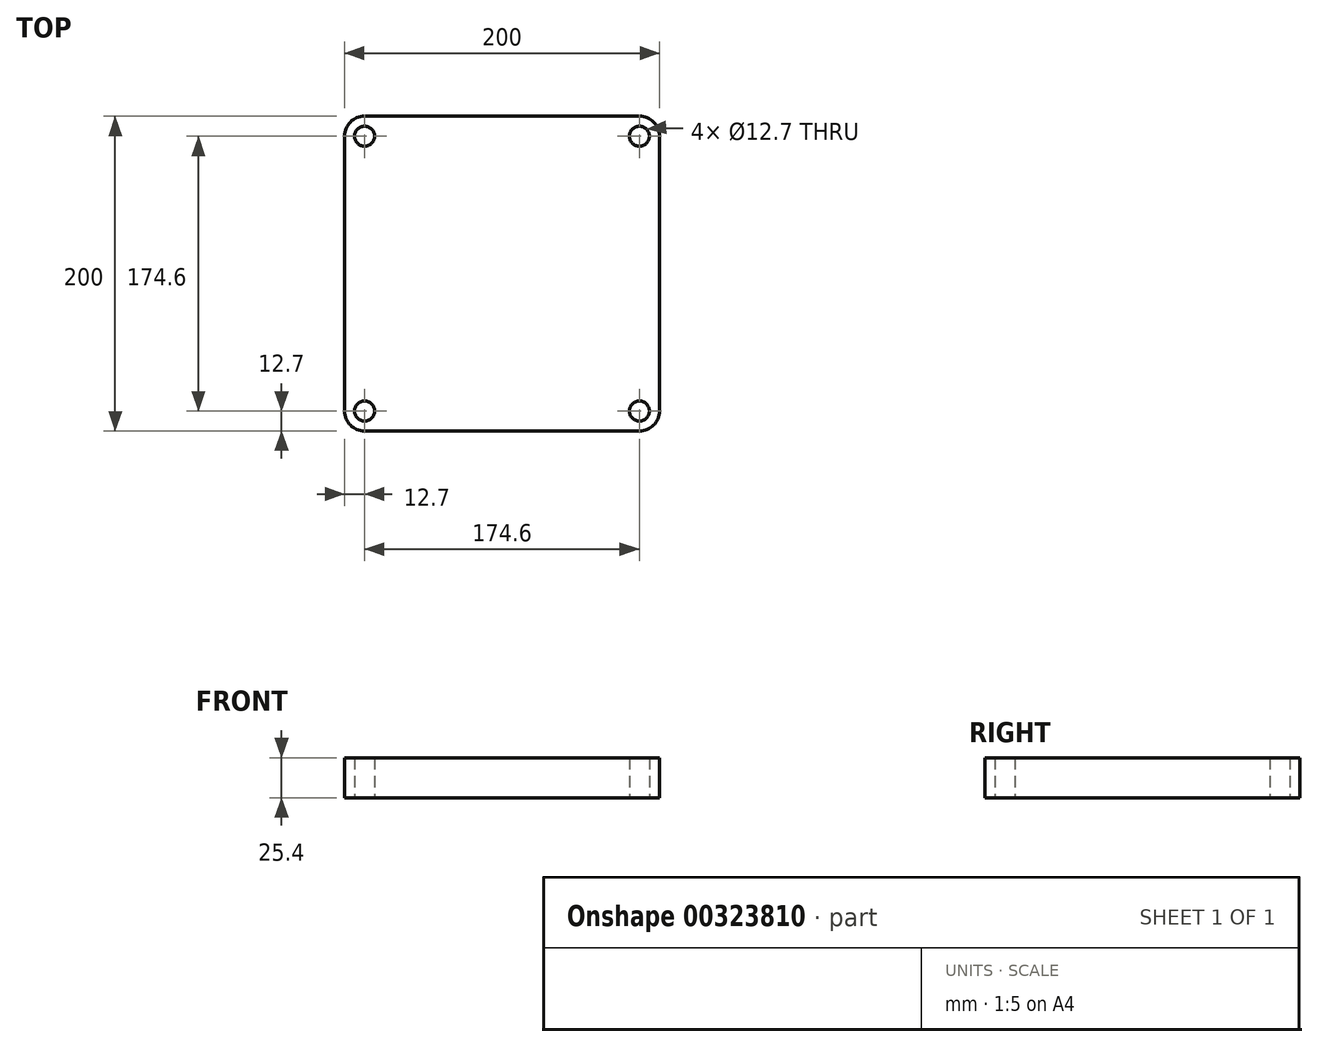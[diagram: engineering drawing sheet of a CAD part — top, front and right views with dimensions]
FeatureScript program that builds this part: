
annotation { "Feature Type Name" : "Feature", "Feature Type Description" : "" }
export const myFeature = defineFeature(function(context is Context, id is Id, definition is map)
    precondition{}
    {
        {
            var Q0;
            Q0=qCreatedBy(makeId("Top.planeOp"),FACE);
            var sketch = newSketch(context, id + "F0", { "sketchPlane" : qUnion([Q0])});
            skLineSegment(sketch, "E0.bottom", {"start": v(-87.3, 100) * mm, "end": v(87.3, 100) * mm});
            skLineSegment(sketch, "E0.top", {"start": v(-87.3, -100) * mm, "end": v(87.3, -100) * mm});
            skLineSegment(sketch, "E0.left", {"start": v(-100, 87.3) * mm, "end": v(-100, -87.3) * mm});
            skLineSegment(sketch, "E0.right", {"start": v(100, 87.3) * mm, "end": v(100, -87.3) * mm});
            skPoint(sketch, "E0.middle", {"position": v(0, 0) * mm});
            skPoint(sketch, "E1.visualSharp", {"position": v(-100, 100) * mm});
            skArc(sketch, "E1.filletArc", {"start": v(-87.3, 100) * mm, "mid": v(-96.28, 96.28) * mm, "end": v(-100, 87.3) * mm});
            skPoint(sketch, "E2.visualSharp", {"position": v(100, 100) * mm});
            skArc(sketch, "E2.filletArc", {"start": v(100, 87.3) * mm, "mid": v(96.28, 96.28) * mm, "end": v(87.3, 100) * mm});
            skPoint(sketch, "E3.visualSharp", {"position": v(100, -100) * mm});
            skArc(sketch, "E3.filletArc", {"start": v(87.3, -100) * mm, "mid": v(96.28, -96.28) * mm, "end": v(100, -87.3) * mm});
            skPoint(sketch, "E4.visualSharp", {"position": v(-100, -100) * mm});
            skArc(sketch, "E4.filletArc", {"start": v(-100, -87.3) * mm, "mid": v(-96.28, -96.28) * mm, "end": v(-87.3, -100) * mm});
            skCircle(sketch, "E5", {"center": v(-87.3, -87.3) * mm, "radius": 6.35 * mm});
            skCircle(sketch, "E6", {"center": v(87.3, -87.3) * mm, "radius": 6.35 * mm});
            skCircle(sketch, "E7", {"center": v(87.3, 87.3) * mm, "radius": 6.35 * mm});
            skCircle(sketch, "E8", {"center": v(-87.3, 87.3) * mm, "radius": 6.35 * mm});
            skSolve(sketch);
        }
        {
            var Q0;
            Q0=makeQuery(id+"F0.imprint","IMPRINT",FACE,{"disambiguationData":[TD([[makeQuery(id+"F0.imprint","IMPRINT",EDGE,{"derivedFrom":sQuery(id+"F0.wireOp",EDGE,"E0.bottom")}),-1.0]])]});
            extrude(context, id + "F1", {"entities" : qUnion([Q0]), "depth" : 25.4 * mm});
        }
    });
